# Revit family: Hekatron_Feststellanlagen_TSG 100_DE_22.01
name_source: partatom
category: Brandmelder
revit_build: Autodesk Revit 2018 (Build: 20190510_1515(x64)
units: mm (PartAtom-declared; Revit-internal decimal feet)

## family parameters
Basisbauteil = Fläche
Beim Laden mit Abzugskörper schneiden = Nein
Bemaßung runder Anschluss = Durchmesser verwenden
Beschriftungsausrichtung beibehalten = Ja
Gemeinsam genutzt = Nein
OmniClass-Nummer = 23.85.30.21
OmniClass-Titel = Environmental Detection/Registration
Raumberechnungspunkt = Nein
Teiletyp = Normal

## types (1)
- TSG 100
    Beschreibung = Akustischer und optischer Signalgeber zum Einsatz in Feststellanlagen an Brand- und Rauchschutztoren zur Signalisierung des Schließvorgangs.
    Betriebsspannung = 24 V DC
    Durchmesser (mm) = 90.0
    Farbe = rot, ähnlich RAL 3001
    Hersteller = Hekatron
    Höhe (mm) = 97.0
    Kabeleinführung = seitlich
    Lautstärke DIN-Ton (dB) = 110.0
    Link zu Ausschreibungstext = https://www.meinhplus.de
    Link zu Produktinformation = https://www.hekatron-planungstools.de
    Link zu ausschreiben.de = http://www.ausschreiben.de
    Material = ABS-FR / PC
    Modell = TSG 100
    Montageart = Aufputz
    Schutzart = IP 65
    Stromaufnahme = max. 55mA
    Typenkommentare = Torsignalgeber TSG 100
    UB A&S Artikel Nummer = 31-6300002-01-02
    URL = https://www.hekatron-brandschutz.de
    Version des BIM Objektes = 22.01
    Vorgabe-Ansicht = 1200 mm
    Zulässige Umgebungstemperatur = -20 °C bis +70 °C

## geometry (parser evidence)
native form markers: Sweep x2
no freeform markers — native parametric forms only
